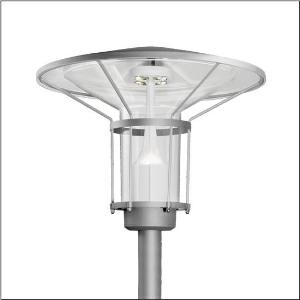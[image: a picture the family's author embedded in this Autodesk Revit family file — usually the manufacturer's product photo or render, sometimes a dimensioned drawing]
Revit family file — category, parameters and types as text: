
# Revit family: laterne_classic_iq___pl1_2s_5xa5245jf14h_d895
name_source: partatom
category: Lighting Fixtures
units: mm (PartAtom-declared; Revit-internal decimal feet)

## family parameters
Cut with Voids When Loaded = No
Host = Face
Light Source = No
Part Type = Normal
Room Calculation Point = No
Round Connector Dimension = Use Diameter
Shared = No

## types (1)
- --- (1 x LED, 2660 lm, 19.3 W, 3000K)
    Apparent Load = 19 VA
    CIE Flux Codes = 21 60 93 97 100
    Color Rendering = 70
    Color Temperature = 3000K
    Default Elevation = 1800 mm
    Description = Lantern Classic iQ, mast luminaire, Module 540 iQ-SR, primary light control with 3 zone facetted reflector, of plastic, silver coated, highly specular, structured, primary optical cover: cover, of PMMA, transparent, light distribution: PL1.2s, light emission: direct distribution, primary light characteristic: symmetric, installation type: post-top, LED, High Power LED, rated luminous flux: 2.670lm, luminous efficacy: 138lm/W, light colour: 730, colour temperature: 3000K, control gear: ECG iQ, control: Auto-Match, Temp-Guard, Lumen-Switch, Night-Set, Smart-Wire, Light-Fading, Desk-Remote (wireless, voltage-free reading and setting of iQ features in the workshop via application-optimized NFC function/RFID function), optimised constant luminous flux control (CLO 2.0), Street-Remote, pre-setting: logarithmic dimming characteristic, with terminal, 6-pole, max. 2.5mm², mains connection: 230..240V, AC, 50/60Hz, start of lifetime: 19W, end of service life: 21W, reduction: 10W, luminaire housing, upper part, of glass-fibre reinforced polyester, coated, Siteco® metallic grey (DB 702S), diameter: 750mm, height: 596mm, spigot size: d x l = 76 x 70mm (post-top) | with reducer (optional accessory) 60 x 70mm, post-top mast mounting element, of diecast aluminium, coated, Siteco® metallic grey (DB 702S), Module 540 iQ-SR, traffic white (RAL 9016), equipment: standard, protection rating (complete): IP65, insulation class (complete): insulation class II (safety insulation), certification: CE, ENEC, VDE, packaging unit: 1 piece

Light Distribution: PL1.2s
    Height = 596 mm
    Lamp = 1 x LED
    Lamp Light Flux = 2660 lm
    Lamp Power = 19.3 W
    Lamp count = 1
    Length = 750 mm
    Luminous efficacy = 138 lm/W
    Manufacturer = Siteco
    ModVariant = No
    Model = 5XA5245JF14H
    Number of Poles = 1
    OnlyDefault = Yes
    Power Factor = 1
    Product Name = Laterne Classic iQ | PL1.2s
    Product group = mast luminaire | pylon top
    ProductGroupID = 6100
    Protection Class = Protection class II
    Protection Degree = IP 65
    RLX_Detail_Level = 1
    RLX_Emergency_Light_Flux = 0 lm
    RLX_Emergency_Type = 0
    RLX_Emergency_Type_DB = No
    RlxData = <blob elided: 62805 chars, md5=9e7911ff>
    Socket = socket
    Standby Power = 0 W
    System Light Flux = 2660 lm
    System Power = 19 W
    Type Comments = factory setting: luminous flux: 100 % | dim-lin: 254 | 403 mA
    Type Image = l_1006052.jpg
    URL = http://relux.com
    VarID = @adj_115669
    Voltage = 0 V
    Weight = 0.00 kg
    Width = 0 mm  [stored 0 ft]

note: [stored X ft] marks values corroborated as IEEE doubles in the binary element streams (Revit-internal decimal feet)

## geometry (parser evidence)
native form markers: Blend x4, Sweep x10
no freeform markers — native parametric forms only
